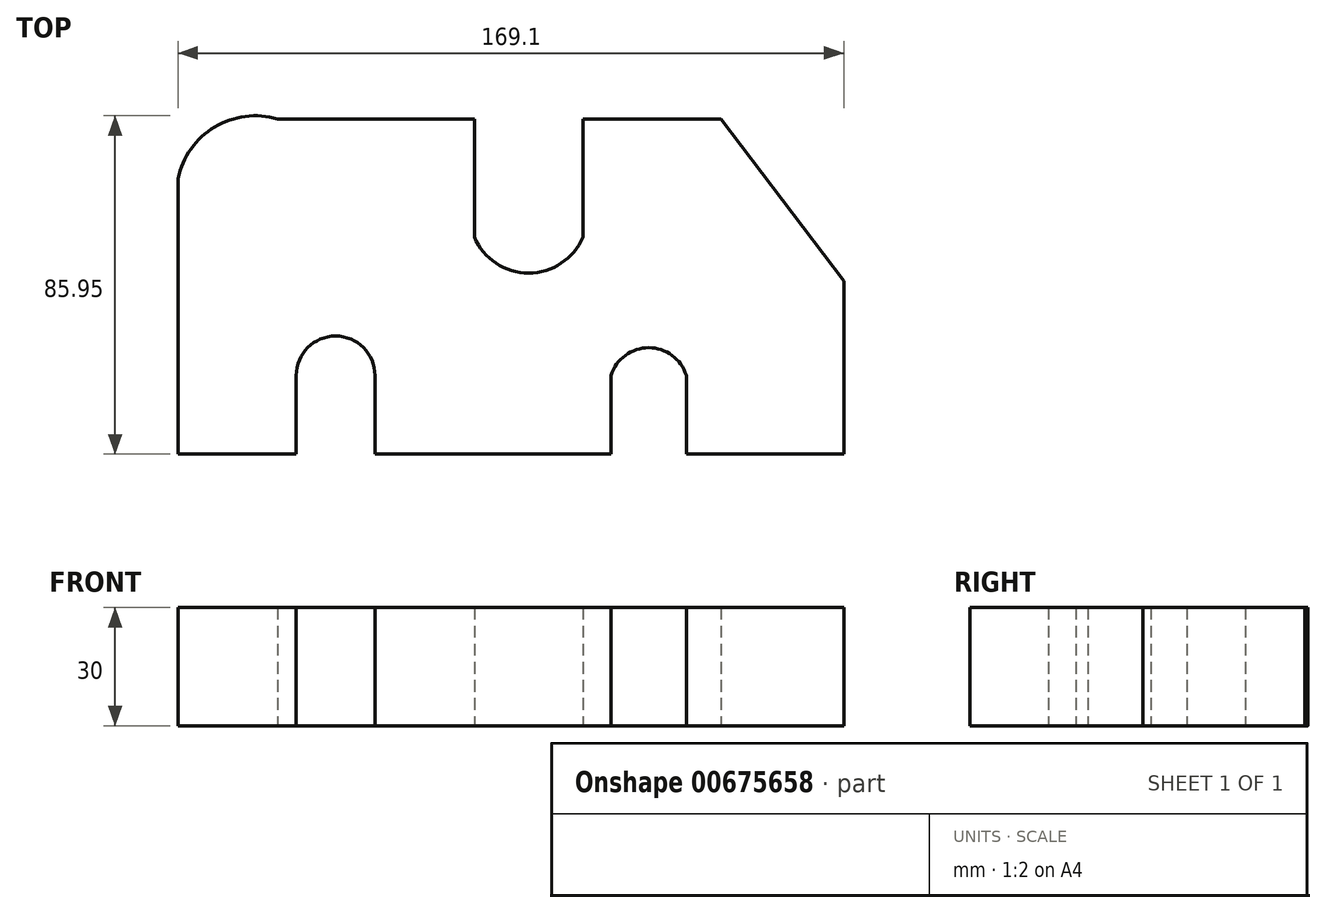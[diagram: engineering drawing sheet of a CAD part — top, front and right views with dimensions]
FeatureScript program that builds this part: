
annotation { "Feature Type Name" : "Feature", "Feature Type Description" : "" }
export const myFeature = defineFeature(function(context is Context, id is Id, definition is map)
    precondition{}
    {
        {
            var Q0;
            Q0=qCreatedBy(makeId("Top.planeOp"),FACE);
            var sketch = newSketch(context, id + "F0", { "sketchPlane" : qUnion([Q0])});
            skArc(sketch, "E0", {"start": v(-41.96, 47.8) * mm, "mid": v(-57.9, 45.77) * mm, "end": v(-67.2, 32.67) * mm});
            skLineSegment(sketch, "E1", {"start": v(-41.96, 47.8) * mm, "end": v(8.04, 47.8) * mm});
            skLineSegment(sketch, "E2", {"start": v(8.04, 47.8) * mm, "end": v(8.04, 17.8) * mm});
            skArc(sketch, "E3", {"start": v(8.04, 17.8) * mm, "mid": v(21.84, 8.68) * mm, "end": v(35.64, 17.8) * mm});
            skLineSegment(sketch, "E4", {"start": v(35.64, 17.8) * mm, "end": v(35.64, 47.8) * mm});
            skLineSegment(sketch, "E5", {"start": v(35.64, 47.8) * mm, "end": v(70.64, 47.8) * mm});
            skLineSegment(sketch, "E6", {"start": v(-67.2, 32.67) * mm, "end": v(-67.2, -37.33) * mm});
            skLineSegment(sketch, "E7", {"start": v(-67.2, -37.33) * mm, "end": v(-37.2, -37.33) * mm});
            skLineSegment(sketch, "E8", {"start": v(-37.2, -37.33) * mm, "end": v(-37.2, -17.33) * mm});
            skArc(sketch, "E9", {"start": v(-17.2, -17.33) * mm, "mid": v(-27.2, -7.33) * mm, "end": v(-37.2, -17.33) * mm});
            skLineSegment(sketch, "E10", {"start": v(-17.2, -17.33) * mm, "end": v(-17.2, -37.33) * mm});
            skLineSegment(sketch, "E11", {"start": v(-17.2, -37.33) * mm, "end": v(42.8, -37.33) * mm});
            skLineSegment(sketch, "E12", {"start": v(42.8, -37.33) * mm, "end": v(42.8, -17.33) * mm});
            skArc(sketch, "E13", {"start": v(61.9, -17.33) * mm, "mid": v(52.35, -10.3) * mm, "end": v(42.8, -17.33) * mm});
            skLineSegment(sketch, "E14", {"start": v(61.9, -17.33) * mm, "end": v(61.9, -37.33) * mm});
            skLineSegment(sketch, "E15", {"start": v(61.9, -37.33) * mm, "end": v(101.9, -37.33) * mm});
            skLineSegment(sketch, "E16", {"start": v(101.9, -37.33) * mm, "end": v(101.9, 6.67) * mm});
            skLineSegment(sketch, "E17", {"start": v(70.64, 47.8) * mm, "end": v(101.9, 6.67) * mm});
            skSolve(sketch);
        }
        {
            var Q0;
            Q0 = qSketchRegion(id + "F0", true);
            extrude(context, id + "F1", {"entities" : qUnion([Q0]), "depth" : 30 * mm, "offsetDistance" : 25 * mm});
        }
    });
